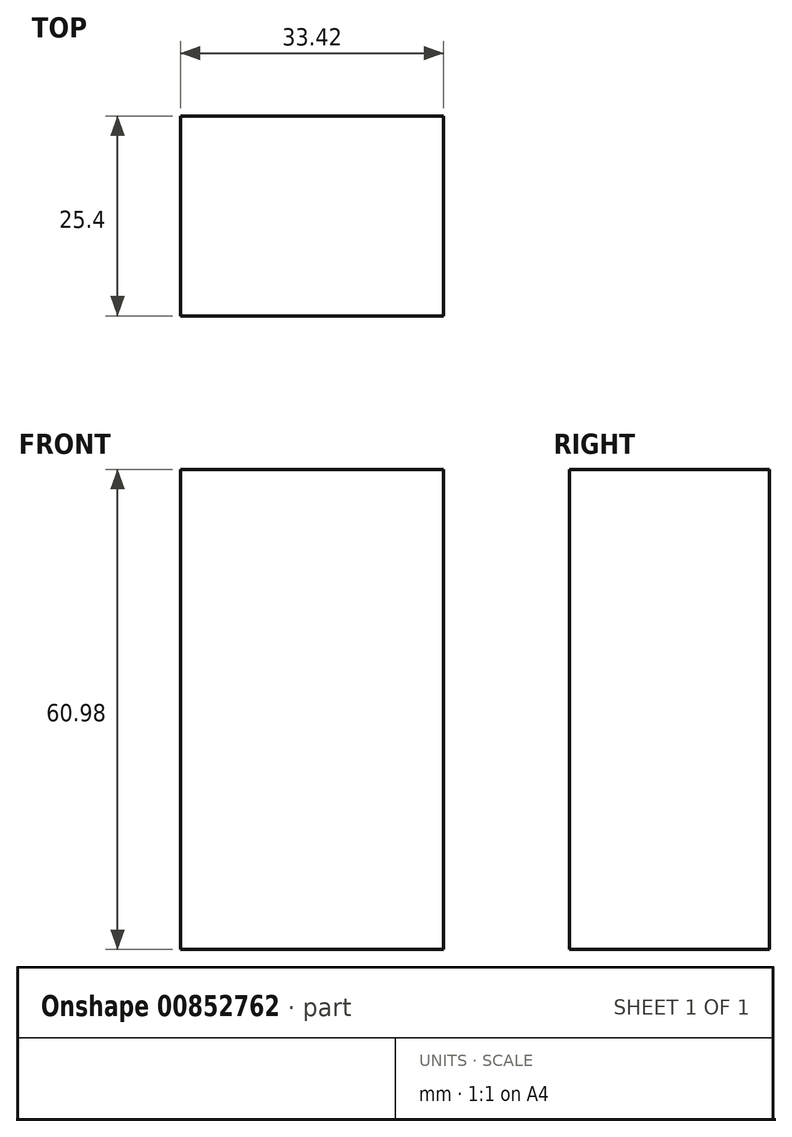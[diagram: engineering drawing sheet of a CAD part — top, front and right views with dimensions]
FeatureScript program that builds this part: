
annotation { "Feature Type Name" : "Feature", "Feature Type Description" : "" }
export const myFeature = defineFeature(function(context is Context, id is Id, definition is map)
    precondition{}
    {
        {
            var Q0;
            Q0=qCreatedBy(makeId("Front.planeOp"),FACE);
            var sketch = newSketch(context, id + "F0", { "sketchPlane" : qUnion([Q0])});
            skLineSegment(sketch, "E0.bottom", {"start": v(-67.07, 41.46) * mm, "end": v(-33.65, 41.46) * mm});
            skLineSegment(sketch, "E0.top", {"start": v(-67.07, -19.52) * mm, "end": v(-33.65, -19.52) * mm});
            skLineSegment(sketch, "E0.left", {"start": v(-67.07, 41.46) * mm, "end": v(-67.07, -19.52) * mm});
            skLineSegment(sketch, "E0.right", {"start": v(-33.65, 41.46) * mm, "end": v(-33.65, -19.52) * mm});
            skSolve(sketch);
        }
        {
            var Q0;
            Q0 = qSketchRegion(id + "F0", true);
            extrude(context, id + "F1", {"entities" : qUnion([Q0]), "depth" : 25.4 * mm, "offsetDistance" : 25.4 * mm});
        }
    });
